# Revit family: Supply-Lavatory-McGuire-Convertible-LFBV2-2166
name_source: partatom
category: Plumbing Fixtures
revit_build: Autodesk Revit 2014 (Build: 20130308_1515(x64)
units: mm (PartAtom-declared; Revit-internal decimal feet)

## types (1)
- LFBV2-2166
    A Length = 1 3/16"
    Assembly Code = D2020300
    B Length = 2 3/16"
    C Length = 1"
    CW Connection = Yes
    CWFU = 0
    Default Elevation = 0"
    Description = McGuire's unique convertible quarter-turn closet supply kit. Furnished with one 1/2" IPS x 3/8" OD brass ball valve, 12 inch copper flexible riser and one steel deep bell flange. All components are chrome plated.
    Finish = Brass-McGuire-Chrome Plated
    HW Connection = Yes
    HWFU = 0
    Hydronic Supply Diameter = 1/2"
    Hydronic Supply Radius = 1/4"
    IAPMO Compliance = cUPC Lead Free
    Manufacturer = McGuire Mfg
    Material = Brass-McGuire-Chrome Plated
    Model = LFBV2-2166
    Outlet Diameter = 3/8"
    Outlet Radius = 3/16"
    Price = Prices may vary. Please consult Manufacturer Representative for most up-to-date price list.
    Riser Length = 12"
    Shipping Weight = 0.72 lb
    Specification = Supply kit shall include one lead free chrome plated, commercial pattern Quarter-Turn Brass Ball Valve with convertible loose key handle, a chrome plated copper riser and one steel deep bell flange.  Inlet shall be 1/2" IPS. Outlet shall be 3/8" OD. Supply kit shall be certified by recognized authority and bear manufacturer and testing mark.
    URL = http://www.mcguiremfg.com
    Vent Connection = No
    WFU = 0
    Warranty Information = 3 Years Limited Warranty
    Waste Connection = No

## geometry (parser evidence)
native form markers: Sweep x1
no freeform markers — native parametric forms only
